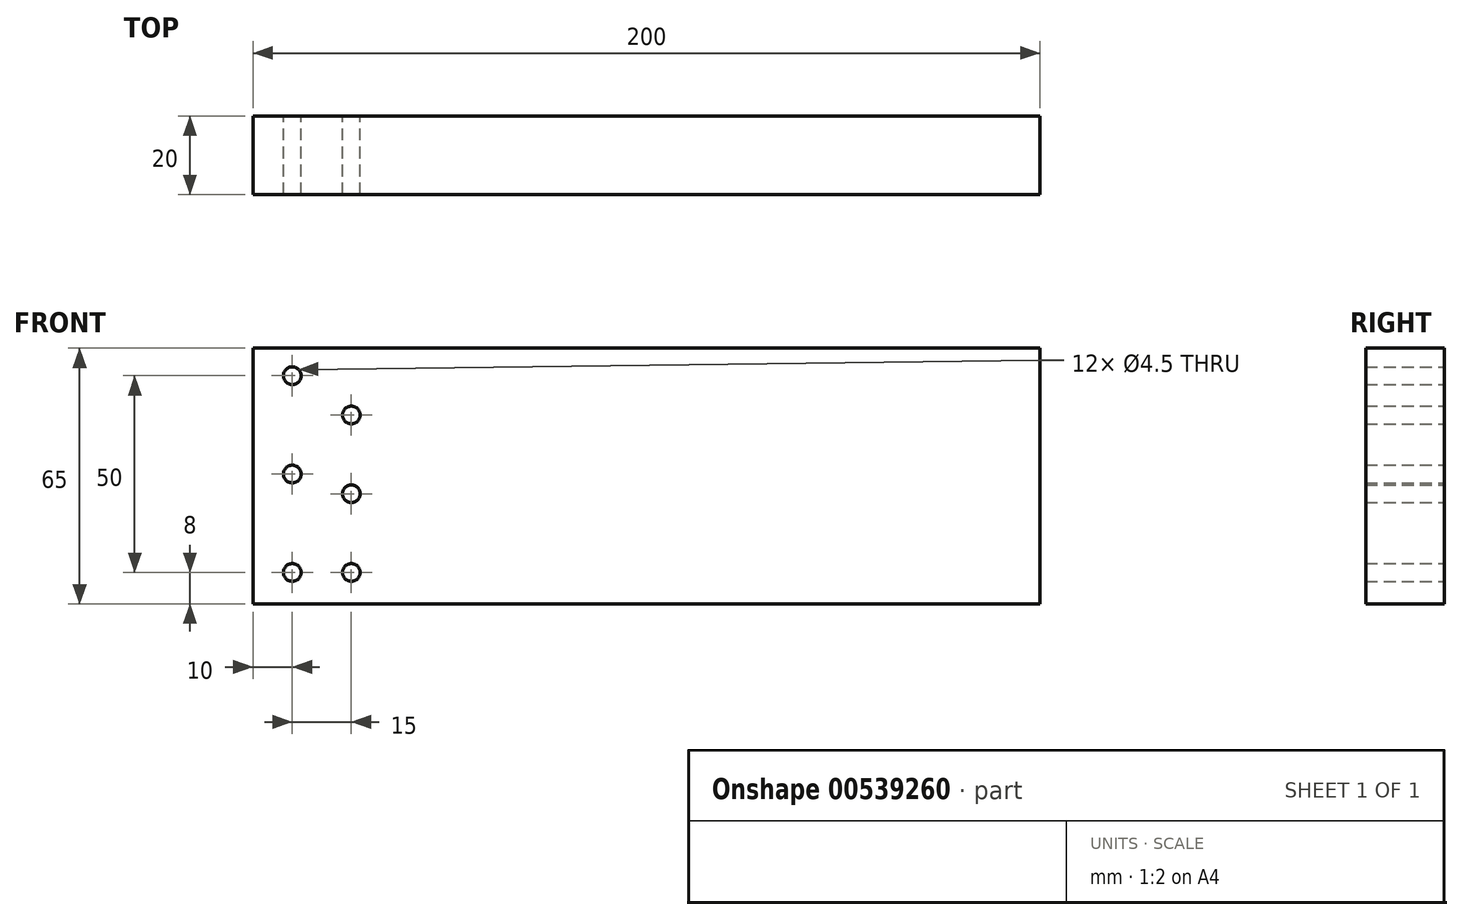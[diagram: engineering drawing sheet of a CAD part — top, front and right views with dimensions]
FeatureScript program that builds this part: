
annotation { "Feature Type Name" : "Feature", "Feature Type Description" : "" }
export const myFeature = defineFeature(function(context is Context, id is Id, definition is map)
    precondition{}
    {
        {
            var Q0;
            Q0=qCreatedBy(makeId("Front.planeOp"),FACE);
            var sketch = newSketch(context, id + "F0", { "sketchPlane" : qUnion([Q0])});
            skLineSegment(sketch, "E0.bottom", {"start": v(0, 0) * mm, "end": v(200, 0) * mm});
            skLineSegment(sketch, "E0.top", {"start": v(0, 65) * mm, "end": v(200, 65) * mm});
            skLineSegment(sketch, "E0.left", {"start": v(0, 0) * mm, "end": v(0, 65) * mm});
            skLineSegment(sketch, "E0.right", {"start": v(200, 0) * mm, "end": v(200, 65) * mm});
            skLineSegment(sketch, "E1", {"start": v(0, 8) * mm, "end": v(10, 8) * mm});
            skLineSegment(sketch, "E2", {"start": v(0, 33) * mm, "end": v(10, 33) * mm});
            skCircle(sketch, "E3", {"center": v(10, 33) * mm, "radius": 2.25 * mm});
            skCircle(sketch, "E4", {"center": v(10, 8) * mm, "radius": 2.25 * mm});
            skLineSegment(sketch, "E5", {"start": v(0, 8) * mm, "end": v(25, 8) * mm});
            skPoint(sketch, "E5.endSnap0", {"position": v(5, 8) * mm});
            skLineSegment(sketch, "E6", {"start": v(25, 8) * mm, "end": v(25, 28) * mm});
            skCircle(sketch, "E7", {"center": v(25, 8) * mm, "radius": 2.25 * mm});
            skCircle(sketch, "E8", {"center": v(25, 28) * mm, "radius": 2.25 * mm});
            skLineSegment(sketch, "E9", {"start": v(25, 28) * mm, "end": v(25, 48) * mm});
            skCircle(sketch, "E10", {"center": v(25, 48) * mm, "radius": 2.25 * mm});
            skLineSegment(sketch, "E11", {"start": v(10, 33) * mm, "end": v(10, 58) * mm});
            skCircle(sketch, "E12", {"center": v(10, 58) * mm, "radius": 2.25 * mm});
            skSolve(sketch);
        }
        {
            var Q0;
            {var subQ3=sQuery(id+"F0.wireOp",EDGE,"E0.bottom");Q0=makeQuery(id+"F0.imprint","IMPRINT",FACE,{"disambiguationData":[TD([[makeQuery(id+"F0.imprint","IMPRINT",EDGE,{"derivedFrom":subQ3}),1.0]])]});}
            extrude(context, id + "F1", {"entities" : qUnion([Q0]), "depth" : 20 * mm, "offsetDistance" : 25 * mm});
        }
    });
